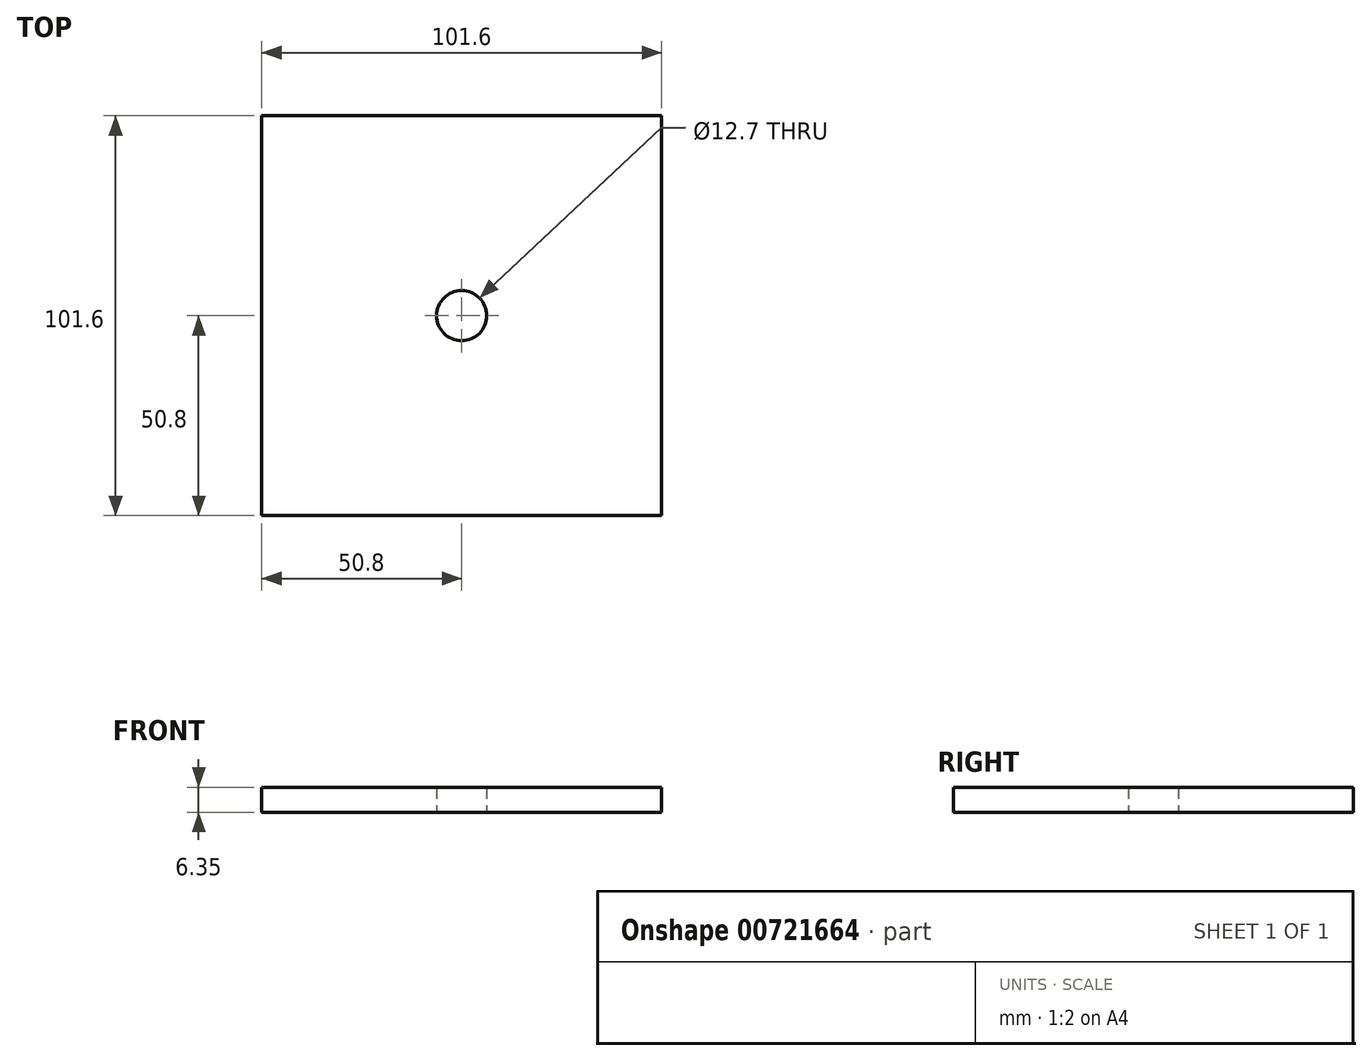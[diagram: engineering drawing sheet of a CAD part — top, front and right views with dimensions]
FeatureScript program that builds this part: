
annotation { "Feature Type Name" : "Feature", "Feature Type Description" : "" }
export const myFeature = defineFeature(function(context is Context, id is Id, definition is map)
    precondition{}
    {
        {
            var Q0;
            Q0=qCreatedBy(makeId("Top.planeOp"),FACE);
            var sketch = newSketch(context, id + "F0", { "sketchPlane" : qUnion([Q0])});
            skLineSegment(sketch, "E0.bottom", {"start": v(50.8, 50.8) * mm, "end": v(-50.8, 50.8) * mm});
            skLineSegment(sketch, "E0.top", {"start": v(50.8, -50.8) * mm, "end": v(-50.8, -50.8) * mm});
            skLineSegment(sketch, "E0.left", {"start": v(50.8, 50.8) * mm, "end": v(50.8, -50.8) * mm});
            skLineSegment(sketch, "E0.right", {"start": v(-50.8, 50.8) * mm, "end": v(-50.8, -50.8) * mm});
            skPoint(sketch, "E0.middle", {"position": v(0, 0) * mm});
            skCircle(sketch, "E1", {"center": v(0, 0) * mm, "radius": 6.35 * mm});
            skSolve(sketch);
        }
        {
            var Q0;
            Q0 = qSketchRegion(id + "F0", true);
            extrude(context, id + "F1", {"entities" : qUnion([Q0]), "depth" : 6.35 * mm, "offsetDistance" : 25.4 * mm});
        }
    });
